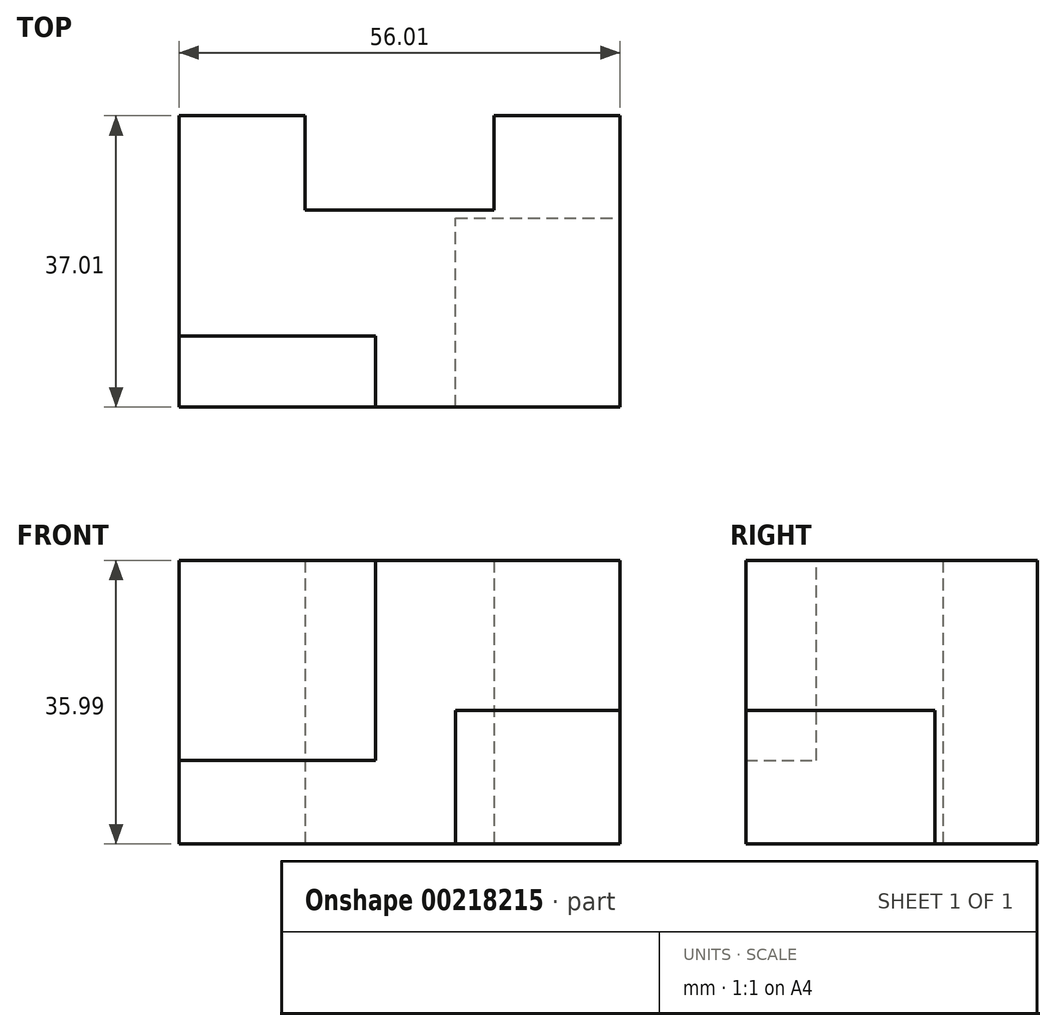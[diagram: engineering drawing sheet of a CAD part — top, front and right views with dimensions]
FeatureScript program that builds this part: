
annotation { "Feature Type Name" : "Feature", "Feature Type Description" : "" }
export const myFeature = defineFeature(function(context is Context, id is Id, definition is map)
    precondition{}
    {
        {
            var Q0;
            Q0=qCreatedBy(makeId("Top.planeOp"),FACE);
            var sketch = newSketch(context, id + "F0", { "sketchPlane" : qUnion([Q0])});
            skLineSegment(sketch, "E0.bottom", {"start": v(0, 0) * mm, "end": v(56, 0) * mm});
            skLineSegment(sketch, "E0.top", {"start": v(0, 37) * mm, "end": v(16, 37) * mm});
            skLineSegment(sketch, "E0.left", {"start": v(0, 0) * mm, "end": v(0, 37) * mm});
            skLineSegment(sketch, "E0.right", {"start": v(56, 0) * mm, "end": v(56, 37) * mm});
            skLineSegment(sketch, "E1.0", {"start": v(16, 25.02) * mm, "end": v(16, 37) * mm});
            skLineSegment(sketch, "E2.0", {"start": v(40, 25.02) * mm, "end": v(40, 37) * mm});
            skLineSegment(sketch, "E3.0", {"start": v(16, 25.02) * mm, "end": v(40, 25.02) * mm});
            skLineSegment(sketch, "E4.trimOffspring", {"start": v(40, 37) * mm, "end": v(56, 37) * mm});
            skSolve(sketch);
        }
        {
            var Q0;
            Q0=makeQuery(id+"F0.imprint","IMPRINT",FACE,{"disambiguationData":[TD([[makeQuery(id+"F0.imprint","IMPRINT",EDGE,{"derivedFrom":sQuery(id+"F0.wireOp",EDGE,"E0.bottom")}),1.0]])]});
            extrude(context, id + "F1", {"entities" : qUnion([Q0]), "depth" : 36 * mm});
        }
        {
            var Q0;
            Q0=makeQuery(id+"F1.opExtrude","CAP_FACE",FACE,{"disambiguationData":[OSD([sQuery(id+"F0.wireOp",EDGE,"E0.bottom"),sQuery(id+"F0.wireOp",EDGE,"E0.top"),sQuery(id+"F0.wireOp",EDGE,"E0.left"),sQuery(id+"F0.wireOp",EDGE,"E0.right"),sQuery(id+"F0.wireOp",EDGE,"E1.0"),sQuery(id+"F0.wireOp",EDGE,"E2.0"),sQuery(id+"F0.wireOp",EDGE,"E3.0"),sQuery(id+"F0.wireOp",EDGE,"E4.trimOffspring")])],"isStart":false});
            var sketch = newSketch(context, id + "F2", { "sketchPlane" : qUnion([Q0])});
            skLineSegment(sketch, "E5.bottom", {"start": v(0, 0) * mm, "end": v(24.97, 0) * mm});
            skLineSegment(sketch, "E5.top", {"start": v(0, 9) * mm, "end": v(24.97, 9) * mm});
            skLineSegment(sketch, "E5.left", {"start": v(0, 0) * mm, "end": v(0, 9) * mm});
            skLineSegment(sketch, "E5.right", {"start": v(24.97, 0) * mm, "end": v(24.97, 9) * mm});
            skSolve(sketch);
        }
        {
            var Q0;
            Q0 = qSketchRegion(id + "F2", true);
            extrude(context, id + "F3", {"entities" : qUnion([Q0]), "operationType" : NewBodyOperationType.REMOVE, "oppositeDirection" : true, "depth" : 25.4 * mm});
        }
        {
            var Q0;
            Q0=makeQuery(id+"F1.opExtrude","SWEPT_FACE",FACE,{"disambiguationData":[OSD([sQuery(id+"F0.wireOp",EDGE,"E0.right")])]});
            var sketch = newSketch(context, id + "F4", { "sketchPlane" : qUnion([Q0])});
            skLineSegment(sketch, "E6.bottom", {"start": v(0, 0) * mm, "end": v(24, 0) * mm});
            skLineSegment(sketch, "E6.top", {"start": v(0, 16.94) * mm, "end": v(24, 16.94) * mm});
            skLineSegment(sketch, "E6.left", {"start": v(0, 0) * mm, "end": v(0, 16.94) * mm});
            skLineSegment(sketch, "E6.right", {"start": v(24, 0) * mm, "end": v(24, 16.94) * mm});
            skSolve(sketch);
        }
        {
            var Q0;
            Q0 = qSketchRegion(id + "F4", true);
            extrude(context, id + "F5", {"entities" : qUnion([Q0]), "operationType" : NewBodyOperationType.REMOVE, "oppositeDirection" : true, "depth" : 20.85 * mm});
        }
    });
